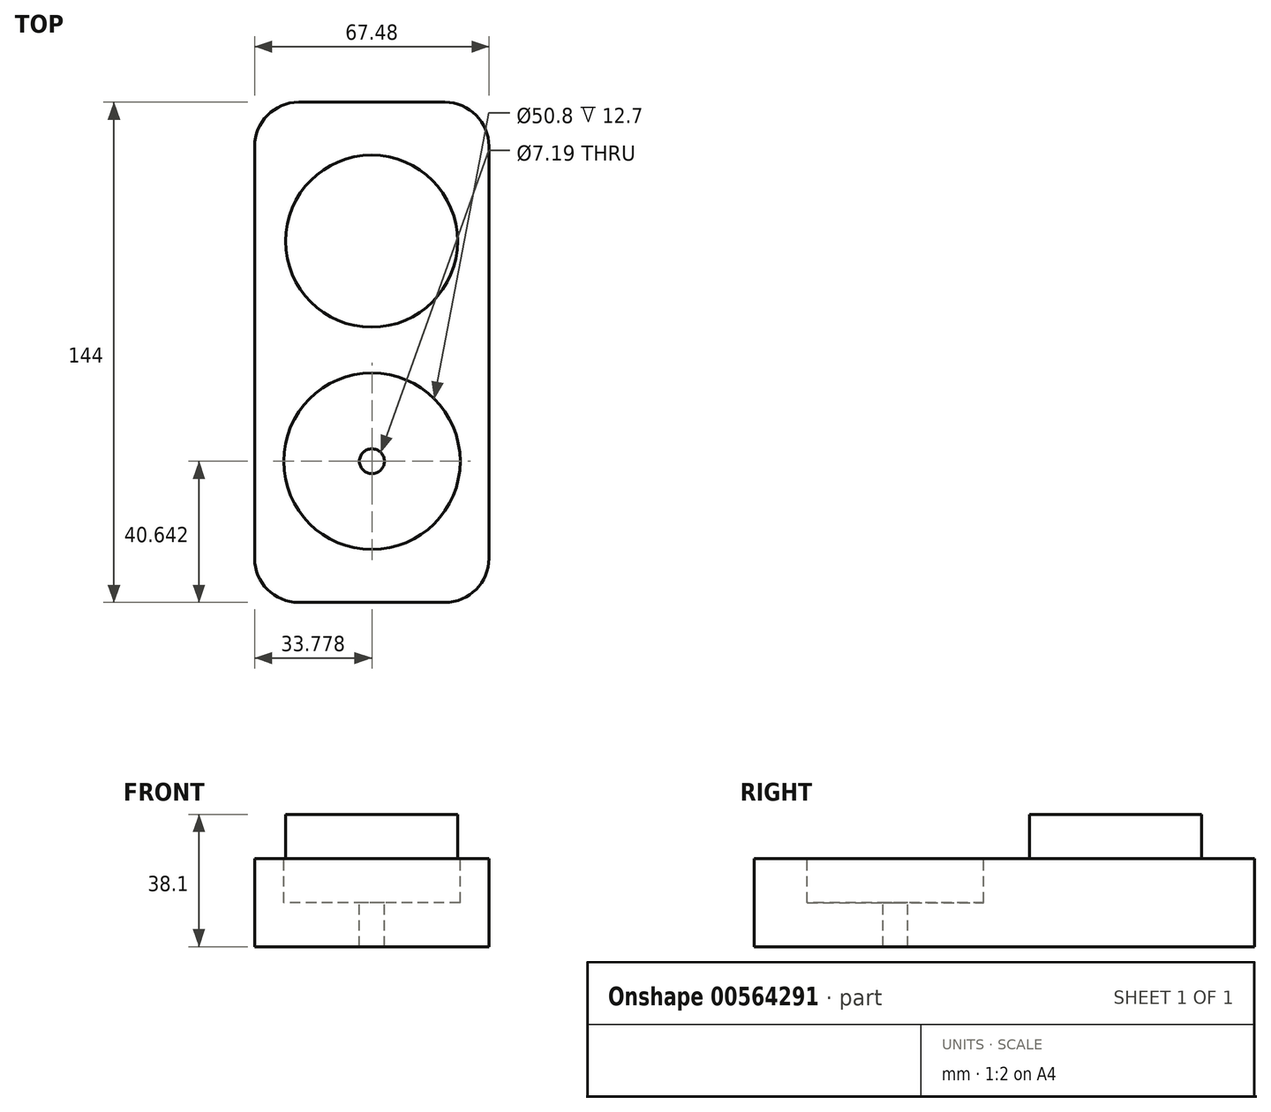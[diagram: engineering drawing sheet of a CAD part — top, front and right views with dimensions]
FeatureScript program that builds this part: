
annotation { "Feature Type Name" : "Feature", "Feature Type Description" : "" }
export const myFeature = defineFeature(function(context is Context, id is Id, definition is map)
    precondition{}
    {
        {
            var Q0;
            Q0=qCreatedBy(makeId("Top.planeOp"),FACE);
            var sketch = newSketch(context, id + "F0", { "sketchPlane" : qUnion([Q0])});
            skLineSegment(sketch, "E0.bottom", {"start": v(-70.98, 70.66) * mm, "end": v(-3.5, 70.66) * mm});
            skLineSegment(sketch, "E0.top", {"start": v(-70.98, -73.34) * mm, "end": v(-3.5, -73.34) * mm});
            skLineSegment(sketch, "E0.left", {"start": v(-70.98, 70.66) * mm, "end": v(-70.98, -73.34) * mm});
            skLineSegment(sketch, "E0.right", {"start": v(-3.5, 70.66) * mm, "end": v(-3.5, -73.34) * mm});
            skSolve(sketch);
        }
        {
            var Q0;
            Q0=makeQuery(id+"F0.imprint","IMPRINT",FACE,{"disambiguationData":[TD([[makeQuery(id+"F0.imprint","IMPRINT",EDGE,{"derivedFrom":sQuery(id+"F0.wireOp",EDGE,"E0.bottom")}),-1.0]])]});
            extrude(context, id + "F1", {"entities" : qUnion([Q0]), "endBound" : BoundingType.SYMMETRIC, "depth" : 25.4 * mm, "offsetDistance" : 25.4 * mm});
        }
        {
            var Q0;
            Q0=makeQuery(id+"F1.opExtrude","SWEPT_EDGE",EDGE,{"disambiguationData":[OSD([sQuery(id+"F0.wireOp",EDGE,"E0.top"),sQuery(id+"F0.wireOp",EDGE,"E0.left")])]});
            var Q1;
            Q1=makeQuery(id+"F1.opExtrude","SWEPT_EDGE",EDGE,{"disambiguationData":[OSD([sQuery(id+"F0.wireOp",EDGE,"E0.top"),sQuery(id+"F0.wireOp",EDGE,"E0.right")])]});
            var Q2;
            Q2=makeQuery(id+"F1.opExtrude","SWEPT_EDGE",EDGE,{"disambiguationData":[OSD([sQuery(id+"F0.wireOp",EDGE,"E0.bottom"),sQuery(id+"F0.wireOp",EDGE,"E0.right")])]});
            var Q3;
            Q3=makeQuery(id+"F1.opExtrude","SWEPT_EDGE",EDGE,{"disambiguationData":[OSD([sQuery(id+"F0.wireOp",EDGE,"E0.bottom"),sQuery(id+"F0.wireOp",EDGE,"E0.left")])]});
            fillet(context, id + "F2", {"entities" : qUnion([Q0, Q1, Q2, Q3]), "radius" : 12.7 * mm, "tangentPropagation" : true, "allowEdgeOverflow" : false});
        }
        {
            var Q0;
            Q0=makeQuery(id+"F1.opExtrude","CAP_FACE",FACE,{"disambiguationData":[OSD([sQuery(id+"F0.wireOp",EDGE,"E0.bottom"),sQuery(id+"F0.wireOp",EDGE,"E0.top"),sQuery(id+"F0.wireOp",EDGE,"E0.left"),sQuery(id+"F0.wireOp",EDGE,"E0.right")])],"isStart":false});
            var sketch = newSketch(context, id + "F3", { "sketchPlane" : qUnion([Q0])});
            skCircle(sketch, "E1", {"center": v(-37.2, -32.7) * mm, "radius": 25.4 * mm});
            skSolve(sketch);
        }
        {
            var Q0;
            Q0=makeQuery(id+"F3.imprint","IMPRINT",FACE,{"disambiguationData":[TD([[makeQuery(id+"F3.imprint","IMPRINT",EDGE,{"derivedFrom":sQuery(id+"F3.wireOp",EDGE,"E1")}),1.0]])]});
            var Q1;
            Q1=makeQuery(id+"F1.opExtrude","CAP_FACE",FACE,{"disambiguationData":[OSD([sQuery(id+"F0.wireOp",EDGE,"E0.bottom"),sQuery(id+"F0.wireOp",EDGE,"E0.top"),sQuery(id+"F0.wireOp",EDGE,"E0.left"),sQuery(id+"F0.wireOp",EDGE,"E0.right")])],"isStart":true});
            extrude(context, id + "F4", {"entities" : qUnion([Q0]), "operationType" : NewBodyOperationType.REMOVE, "oppositeDirection" : true, "depth" : 12.7 * mm, "endBoundEntityFace" : qUnion([Q1]), "offsetDistance" : 25.4 * mm});
        }
        {
            var Q0;
            Q0=makeQuery(id+"F4.boolean.opBoolean","COPY",FACE,{"derivedFrom":makeQuery(id+"F4.opExtrude","CAP_FACE",FACE,{"disambiguationData":[OSD([sQuery(id+"F3.wireOp",EDGE,"E1")])],"isStart":false})});
            var sketch = newSketch(context, id + "F5", { "sketchPlane" : qUnion([Q0])});
            skCircle(sketch, "E2", {"center": v(-37.2, -32.7) * mm, "radius": 3.6 * mm});
            skSolve(sketch);
        }
        {
            var Q0;
            Q0=makeQuery(id+"F5.imprint","IMPRINT",FACE,{"disambiguationData":[TD([[makeQuery(id+"F5.imprint","IMPRINT",EDGE,{"derivedFrom":sQuery(id+"F5.wireOp",EDGE,"E2")}),1.0]])]});
            var Q1;
            Q1=makeQuery(id+"F1.opExtrude","CAP_FACE",FACE,{"disambiguationData":[OSD([sQuery(id+"F0.wireOp",EDGE,"E0.bottom"),sQuery(id+"F0.wireOp",EDGE,"E0.top"),sQuery(id+"F0.wireOp",EDGE,"E0.left"),sQuery(id+"F0.wireOp",EDGE,"E0.right")])],"isStart":true});
            extrude(context, id + "F6", {"entities" : qUnion([Q0]), "operationType" : NewBodyOperationType.REMOVE, "endBound" : BoundingType.UP_TO_SURFACE, "oppositeDirection" : true, "depth" : 25.4 * mm, "endBoundEntityFace" : qUnion([Q1]), "offsetDistance" : 25.4 * mm});
        }
        {
            var Q0;
            Q0=makeQuery(id+"F3.imprint","IMPRINT",FACE,{"disambiguationData":[TD([[makeQuery(id+"F3.imprint","IMPRINT",EDGE,{"derivedFrom":sQuery(id+"F3.wireOp",EDGE,"E1")}),-1.0]])]});
            var sketch = newSketch(context, id + "F7", { "sketchPlane" : qUnion([Q0])});
            skCircle(sketch, "E3", {"center": v(-37.3, 30.65) * mm, "radius": 24.77 * mm});
            skSolve(sketch);
        }
        {
            var Q0;
            Q0 = qSketchRegion(id + "F7", true);
            extrude(context, id + "F8", {"entities" : qUnion([Q0]), "operationType" : NewBodyOperationType.ADD, "depth" : 12.7 * mm, "offsetDistance" : 25.4 * mm});
        }
    });
